# Revit family: RBOC-LR-LG1UW2-6WLEDSB
name_source: partatom
category: Lighting Fixtures
units: mm (PartAtom-declared; Revit-internal decimal feet)

## family parameters
Cut with Voids When Loaded = No
Host = Face
Light Source = Yes
Maintain Annotation Orientation = No
Part Type = Normal
Room Calculation Point = No
Round Connector Dimension = Use Diameter
Shared = No

## types (2) — shared parameters
BODY MATERIAL = BODY MATERIAL
Color Filter = 16777215
Default Elevation = 4' - 0"
Dimming Lamp Color Temperature Shift = <None>
Emit from Line Length = 2' - 0"
FACE MATERIAL = FACE MATERIAL
LENS MATERIAL = LENS MATERIAL
Lamp = LED
Manufacturer = BEGHELLI
Model = RBOCLRLG1UW2-6WLEDSB
Photometric Web File = RBOLED-6W.ies
Tilt Angle = 0.00°
Type Image = RBOC IMAGE.jpg
Wattage Comments = 12 W (2X6W)

## per-type parameters (varying)
| type | LETTER MATERIAL |
| RBOCLR1UW2-6WLED SB | LETTER MATERIAL RED |
| RBOCLG1UW2-6WLED SB | LETTER MATERIAL GREEN |

## geometry (parser evidence)
native form markers: Sweep x10
no freeform markers — native parametric forms only
